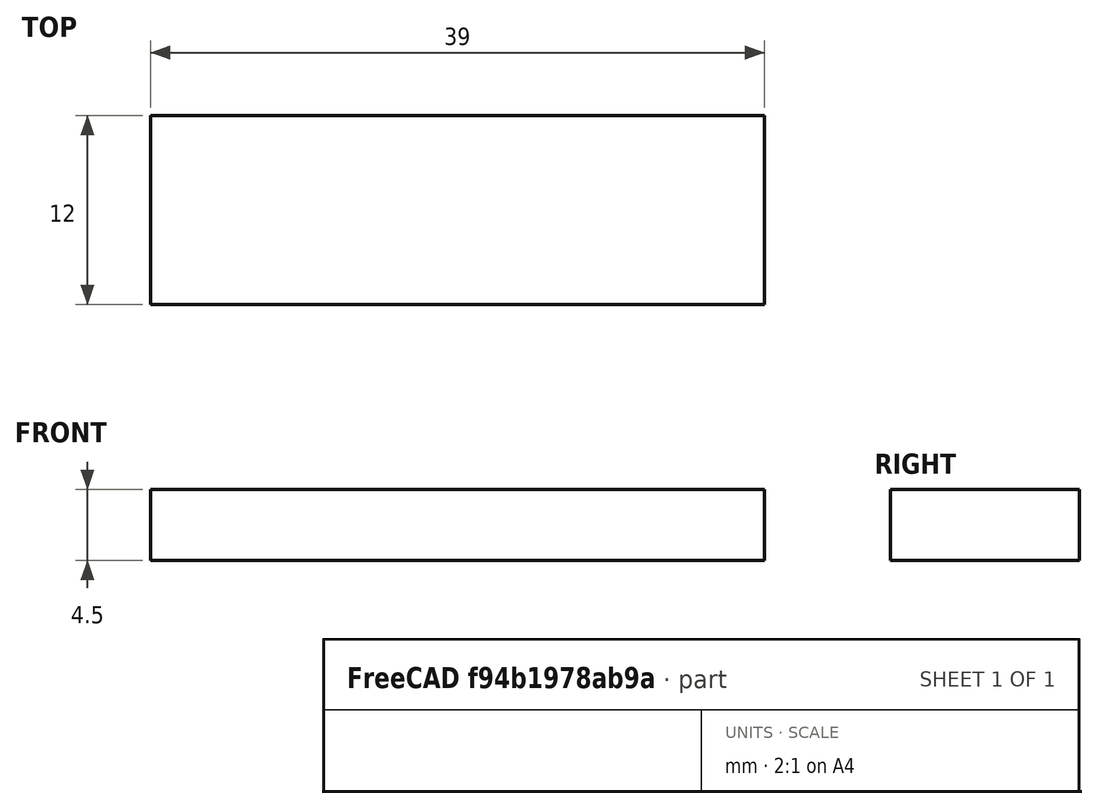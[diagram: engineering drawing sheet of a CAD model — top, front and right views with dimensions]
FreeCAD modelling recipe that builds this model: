
FCSTD DOCUMENT  (FreeCAD 1.0R39109 (Git))
Label: Suporte_tela_OLED
License: All rights reserved
LicenseURL: https://en.wikipedia.org/wiki/All_rights_reserved
objects: Sketcher::SketchObject×2, PartDesign::Body×2, PartDesign::Pad×1, PartDesign::ShapeBinder×1
note: 10 computed .brp shape members not serialized (recipe doc carries the construction recipe); baked Part::Feature solids carry a one-line shape summary decoded from their .brp

FEATURE [Sketcher::SketchObject] Sketch
  ArcFitTolerance = 1e-06
  AttachmentSupport = -> [XY_Plane]
  FullyConstrained = true
  MakeInternals = false
  MapMode = 5
  sketch-geometry (5):
    g0: LineSegment StartX=19.5 StartY=-6 StartZ=0 EndX=19.5 EndY=6 EndZ=0
    g1: LineSegment StartX=19.5 StartY=6 StartZ=0 EndX=-19.5 EndY=6 EndZ=0
    g2: LineSegment StartX=-19.5 StartY=6 StartZ=0 EndX=-19.5 EndY=-6 EndZ=0
    g3: LineSegment StartX=-19.5 StartY=-6 StartZ=0 EndX=19.5 EndY=-6 EndZ=0
    g4: GeomPoint [constr] X=0 Y=0 Z=0
  constraints (12):
    c: Coincident(g0,g1)
    c: Coincident(g1,g2)
    c: Coincident(g2,g3)
    c: Coincident(g3,g0)
    c: Vertical(g0)
    c: Vertical(g2)
    c: Horizontal(g1)
    c: Horizontal(g3)
    c: Symmetric(g2,g0,g4)
    c: Coincident(g4,g-1)
    c: DistanceX(g1,g1) = 39
    c: DistanceY(g0,g0) = 12
FEATURE [PartDesign::Pad] Pad  label="PCB OLED"
  Direction = (0,0,1)
  Length = 4.5
  Length2 = 10
  Profile = -> Sketch
  ReferenceAxis = -> Sketch [N_Axis]
  Refine = true
  Suppressed = false
  Type = 0
FEATURE [PartDesign::Body] Body  label="PCB_OLED"
  AllowCompound = false
  Group = -> [Sketch,Pad]
  Origin = -> Origin
  Tip = -> Pad
FEATURE [PartDesign::ShapeBinder] CopyPad
  TraceSupport = false
FEATURE [Sketcher::SketchObject] Sketch001
  ArcFitTolerance = 1e-06
  AttachmentSupport = -> [CopyPad]
  FullyConstrained = true
  MakeInternals = false
  MapMode = 5
  Placement = pos=(0,-6,0) rot=(1,0,0;1.5708rad)
FEATURE [PartDesign::Body] Body001  label="Proteção"
  AllowCompound = false
  Group = -> [CopyPad,Sketch001]
  Origin = -> Origin001
